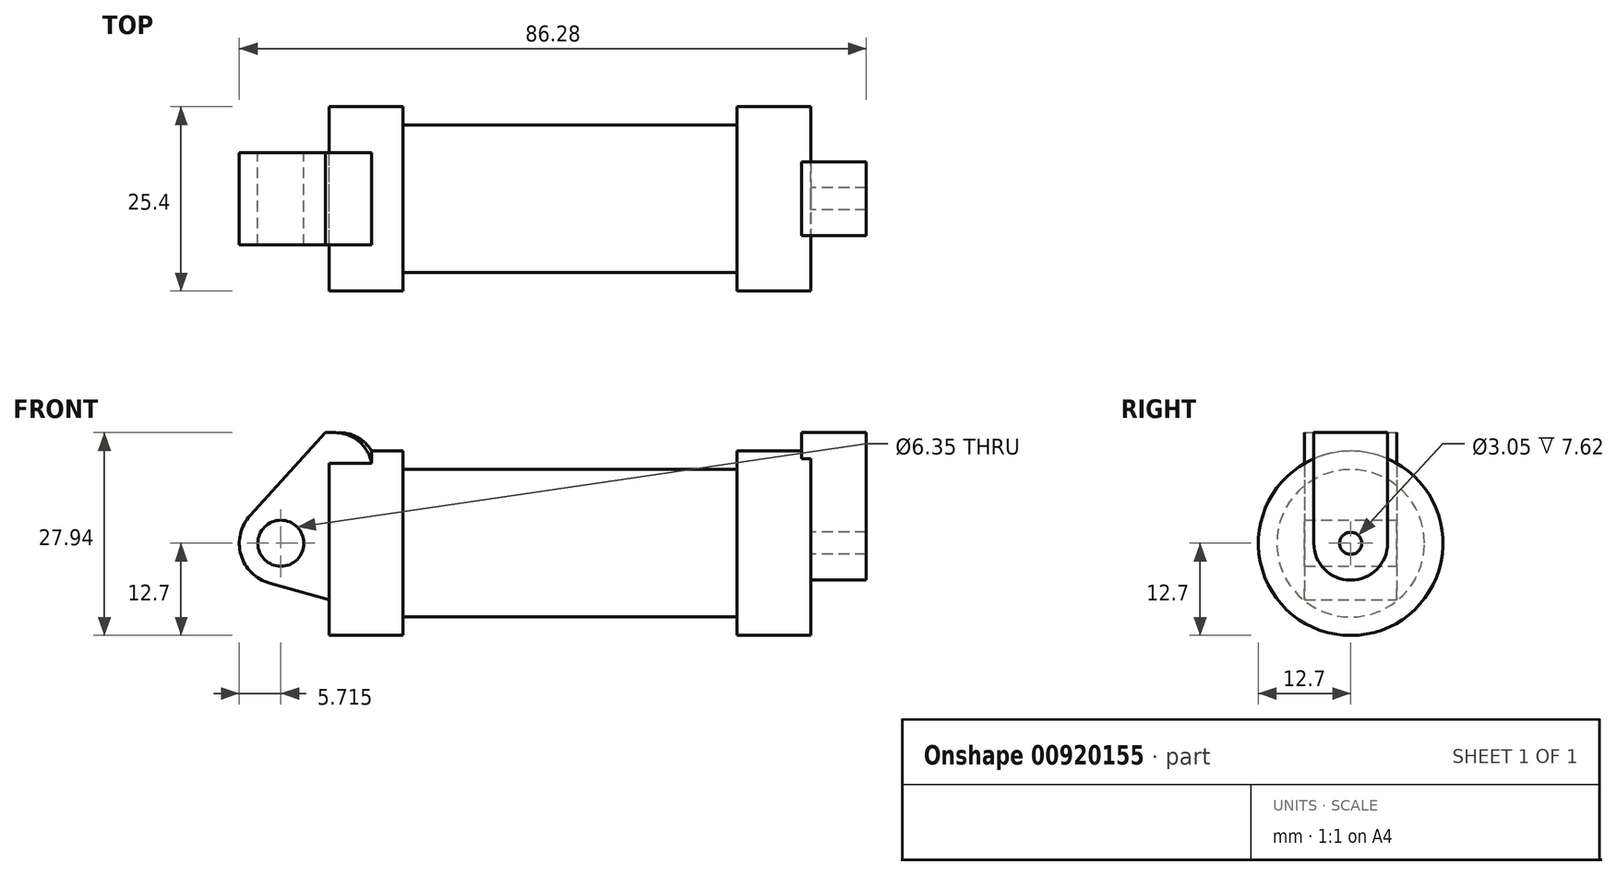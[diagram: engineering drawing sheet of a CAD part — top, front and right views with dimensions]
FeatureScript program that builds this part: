
annotation { "Feature Type Name" : "Feature", "Feature Type Description" : "" }
export const myFeature = defineFeature(function(context is Context, id is Id, definition is map)
    precondition{}
    {
        {
            var Q0;
            Q0=qCreatedBy(makeId("Front.planeOp"),FACE);
            var sketch = newSketch(context, id + "F0", { "sketchPlane" : qUnion([Q0])});
            skLineSegment(sketch, "E0", {"start": v(0, 0) * mm, "end": v(0, 12.7) * mm});
            skLineSegment(sketch, "E1", {"start": v(0, 12.7) * mm, "end": v(10.16, 12.7) * mm});
            skLineSegment(sketch, "E2", {"start": v(10.16, 12.7) * mm, "end": v(10.16, 10.16) * mm});
            skLineSegment(sketch, "E3", {"start": v(10.16, 10.16) * mm, "end": v(56.13, 10.16) * mm});
            skLineSegment(sketch, "E4", {"start": v(56.13, 10.16) * mm, "end": v(56.13, 12.7) * mm});
            skLineSegment(sketch, "E5", {"start": v(56.13, 12.7) * mm, "end": v(66.3, 12.7) * mm});
            skLineSegment(sketch, "E6", {"start": v(66.3, 12.7) * mm, "end": v(66.3, 0) * mm});
            skLineSegment(sketch, "E7", {"start": v(66.3, 0) * mm, "end": v(0, 0) * mm});
            skLineSegment(sketch, "E8", {"start": v(5.84, 15.24) * mm, "end": v(-0.5, 15.24) * mm});
            skLineSegment(sketch, "E9", {"start": v(-0.5, 15.24) * mm, "end": v(-10.88, 3.85) * mm});
            skLineSegment(sketch, "E10", {"start": v(0, 0) * mm, "end": v(-6.65, 0) * mm});
            skCircle(sketch, "E11", {"center": v(-6.65, 0) * mm, "radius": 5.72 * mm});
            skCircle(sketch, "E12", {"center": v(-6.65, 0) * mm, "radius": 3.18 * mm});
            skLineSegment(sketch, "E13", {"start": v(5.84, 15.24) * mm, "end": v(5.84, -9.4) * mm});
            skLineSegment(sketch, "E14", {"start": v(5.84, -9.4) * mm, "end": v(-8.18, -5.5) * mm});
            skSolve(sketch);
        }
        {
            var Q0;
            {var subQ0=sQuery(id+"F0.wireOp",EDGE,"E2");Q0=makeQuery(id+"F0.imprint","IMPRINT",FACE,{"disambiguationData":[TD([[makeQuery(id+"F0.imprint","IMPRINT",EDGE,{"derivedFrom":subQ0}),-1.0]])]});}
            var Q1;
            {var subQ0=sQuery(id+"F0.wireOp",EDGE,"E0");Q1=makeQuery(id+"F0.imprint","IMPRINT",FACE,{"disambiguationData":[TD([[makeQuery(id+"F0.imprint","IMPRINT",EDGE,{"derivedFrom":subQ0}),-1.0]])]});}
            var Q2;
            Q2=sQuery(id+"F0.wireOp",EDGE,"E7");
            revolve(context, id + "F1", {"surfaceOperationType" : NewSurfaceOperationType.NEW, "entities" : qUnion([Q0, Q1]), "axis" : qUnion([Q2]), "revolveType" : RevolveType.FULL});
        }
        {
            var Q0;
            Q0=makeQuery(id+"F1.opRevolve","SWEPT_FACE",FACE,{"disambiguationData":[OSD([sQuery(id+"F0.wireOp",EDGE,"E6")])]});
            var sketch = newSketch(context, id + "F2", { "sketchPlane" : qUnion([Q0])});
            skCircle(sketch, "E15", {"center": v(0, 0) * mm, "radius": 5.08 * mm});
            skCircle(sketch, "E16", {"center": v(0, 0) * mm, "radius": 1.52 * mm});
            skLineSegment(sketch, "E17", {"start": v(5.08, 0) * mm, "end": v(5.08, 15.24) * mm});
            skLineSegment(sketch, "E18.MirrorCS", {"start": v(-5.08, 0) * mm, "end": v(-5.08, 15.24) * mm});
            skLineSegment(sketch, "E19", {"start": v(-5.08, 15.24) * mm, "end": v(5.08, 15.24) * mm});
            skSolve(sketch);
        }
        {
            var Q0;
            Q0 = qSketchRegion(id + "F2", true);
            extrude(context, id + "F3", {"entities" : qUnion([Q0]), "operationType" : NewBodyOperationType.ADD, "depth" : 7.62 * mm, "offsetDistance" : 25.4 * mm, "hasSecondDirection" : true, "secondDirectionOppositeDirection" : true, "secondDirectionDepth" : 1.27 * mm});
        }
        {
            var Q0;
            {var subQ0=sQuery(id+"F0.wireOp",EDGE,"E14");Q0=makeQuery(id+"F0.imprint","IMPRINT",FACE,{"disambiguationData":[TD([[makeQuery(id+"F0.imprint","IMPRINT",EDGE,{"derivedFrom":subQ0}),-1.0]])]});}
            var Q1;
            {var subQ1=sQuery(id+"F0.wireOp",EDGE,"E0");Q1=makeQuery(id+"F0.imprint","IMPRINT",FACE,{"disambiguationData":[TD([[makeQuery(id+"F0.imprint","IMPRINT",EDGE,{"derivedFrom":subQ1}),1.0]])]});}
            var Q2;
            {var subQ5=sQuery(id+"F0.wireOp",EDGE,"E12");Q2=makeQuery(id+"F0.imprint","IMPRINT",FACE,{"disambiguationData":[TD([[makeQuery(id+"F0.imprint","IMPRINT",EDGE,{"derivedFrom":subQ5}),-1.0]])]});}
            var Q3;
            {var subQ0=sQuery(id+"F0.wireOp",EDGE,"E0");Q3=makeQuery(id+"F0.imprint","IMPRINT",FACE,{"disambiguationData":[TD([[makeQuery(id+"F0.imprint","IMPRINT",EDGE,{"derivedFrom":subQ0}),-1.0]])]});}
            extrude(context, id + "F4", {"entities" : qUnion([Q0, Q1, Q2, Q3]), "operationType" : NewBodyOperationType.ADD, "endBound" : BoundingType.SYMMETRIC, "depth" : 12.7 * mm, "offsetDistance" : 25.4 * mm, "hasSecondDirection" : true, "secondDirectionOppositeDirection" : true, "secondDirectionDepth" : 25.4 * mm});
        }
        {
            var Q0;
            Q0=makeQuery(id+"F4.opExtrude","SWEPT_EDGE",EDGE,{"disambiguationData":[OSD([sQuery(id+"F0.wireOp",EDGE,"E8"),sQuery(id+"F0.wireOp",EDGE,"E13")])]});
            fillet(context, id + "F5", {"entities" : qUnion([Q0]), "radius" : 5.08 * mm, "tangentPropagation" : true, "allowEdgeOverflow" : false});
        }
    });
